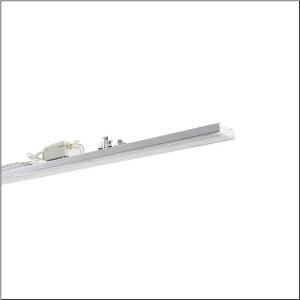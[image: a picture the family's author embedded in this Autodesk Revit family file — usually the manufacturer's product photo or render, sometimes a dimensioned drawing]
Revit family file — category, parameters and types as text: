
# Revit family: licross_r__21_recessed_mo_52tl12dn4axg3s_be2a
name_source: partatom
category: Lighting Fixtures
units: mm (PartAtom-declared; Revit-internal decimal feet)

## family parameters
Cut with Voids When Loaded = No
Host = Face
Light Source = No
Part Type = Normal
Room Calculation Point = No
Round Connector Dimension = Use Diameter
Shared = No

## types (1)
- --- (1 x LED, 950 lm, 6.7 W, 4000K)
    Apparent Load = 7 VA
    CIE Flux Codes = 72 92 99 100 100
    Color Rendering = 80
    Color Temperature = 4000K
    Default Elevation = 1800 mm
    Description = Licross® 21 Recessed MO, luminaire insert, of sheet steel, galvanised, coil coated, white, length: 1.500mm, width: 66mm, height: 67mm, LED rated luminous flux: 10.280lm, light colour: 840, control gear: DALI 2, with plug, 6-pole, with phase selection, for trunking rail, 14-core, mains connection: 220..240V, AC, 50/60Hz, rated input power: 62W, halogen-free wiring, for emergency light function, for trunking rail, 14-core, converter,control gear: single battery element, battery: LiFeP04, 9Ah, primary optical cover: cover, of PMMA, light emission: direct distribution, primary light characteristic: symmetric, protection rating (complete): IP40, insulation class (complete): insulation class I (protective earthing), certification: CE, UKCA, protection symbol: D if used in an environment without relevant dust loads with corresponding accessories, impact resistance: IK06, permissible ambient temperature for indoor applications: +5..+35°C, standard: EN 60598-2-22, LABS conformity tested according to VDMA 24364:2018-05, reducing of maximum allowable ambient temperature of 5°C with ceiling mounting, corresponds to IFS (International Featured Standards) requirements for safety and quality in the food industry, packaging unit: 1 piece
    Height = 58 mm
    Lamp = 1 x LED
    Lamp Light Flux = 950 lm
    Lamp Power = 6.7 W
    Lamp count = 1
    Length = 1500 mm
    Luminous efficacy = 142 lm/W
    Manufacturer = Siteco
    ModVariant = No
    Model = 52TL12DN4AXG3S
    Mounting Place = Ceiling
    Mounting Type = Pendant
    Number of Poles = 1
    OnlyDefault = Yes
    Power Factor = 1
    Product Name = Licross® 21 Recessed MO
    Product group = luminaire insert
    ProductGroupID = 901
    Protection Class = Protection class I
    Protection Degree = IP 40
    RLX_Detail_Level = 1
    RLX_Emergency_Light_Flux = 0 lm
    RLX_Emergency_Type = 0
    RLX_Emergency_Type_DB = No
    RlxData = <blob elided: 25005 chars, md5=2ceaf4c2>
    Socket = socket
    Standby Power = 0 W
    System Light Flux = 950 lm
    System Power = 7 W
    Type Comments = : emergency light operation: 3 h
    Type Image = l_1296930.jpg
    URL = http://relux.com
    VarID = @adj_040187
    Voltage = 0 V
    Weight = 0.00 kg
    Width = 66 mm

## geometry (parser evidence)
native form markers: Blend x4, Sweep x12
no freeform markers — native parametric forms only
